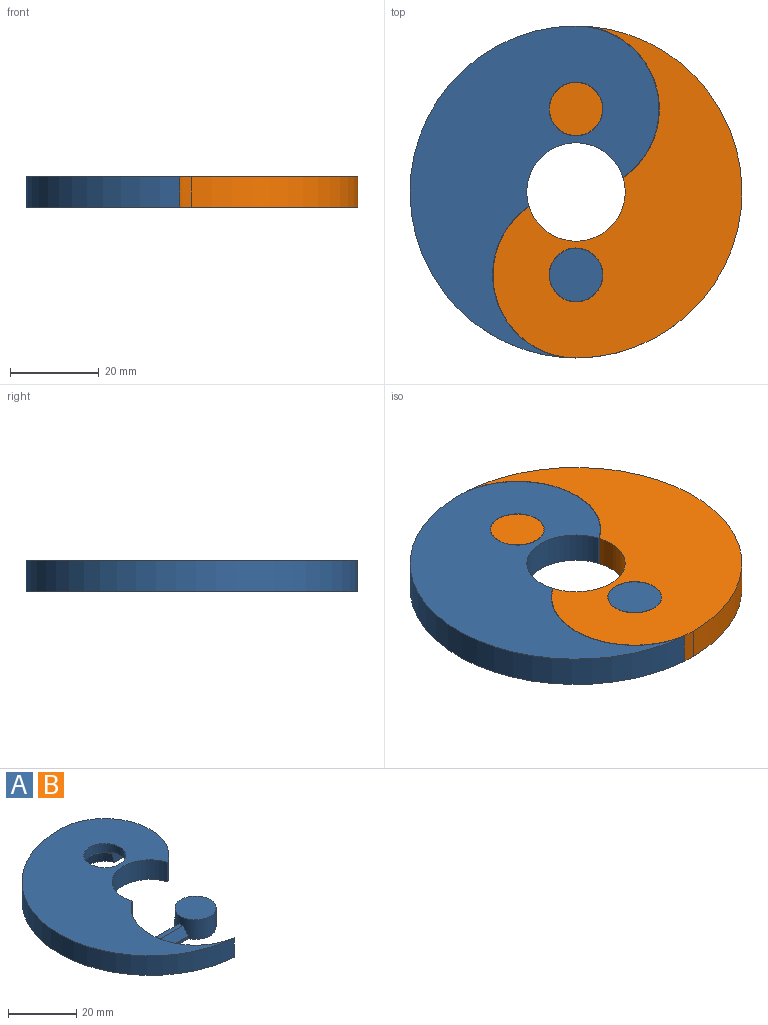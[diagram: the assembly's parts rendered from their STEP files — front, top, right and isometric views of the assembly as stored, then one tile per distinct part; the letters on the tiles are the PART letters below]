
ASSEMBLY  parts=2 mates=1
PART A: 28 faces, bbox 56.3x74.9x7 mm
  f0: plane 13.21x5.1mm, normal (0,0,-1), area 65.2mm2, adj f4,f11,f12,f27
  f1: plane 74.9x56.08mm, normal (0,0,-1), area 1974.4mm2, adj f3,f4,f5,f6,f8,f9,f11,f12
  f2: plane 74.9x56.25mm, normal (0,0,1), area 1893.9mm2, adj f3,f4,f5,f15,f18,f27
  f3: cylinder r=11.1mm len=21.7mm, axis (0,0,-1), area 244.1mm2, adj f1,f2,f4,f18
  f4: cylinder r=18.75mm len=34.21mm, axis (0,0,-1), area 312mm2, adj f0,f1,f2,f3,f5,f11,f12
  f5: cylinder r=37.5mm len=74.9mm, axis (0,0,-1), area 805.5mm2, adj f1,f2,f4,f15
  f6: cylinder r=6mm len=12mm, axis (0,0,-1), area 248.8mm2, adj f1,f7,f8,f9,f10,f13,f14
  f7: plane 12x12mm, normal (0,0,1), area 113.1mm2, adj f6
  f8: plane 13.13x1mm, normal (0,-1,0), area 13.1mm2, adj f1,f6,f14,f19
  f9: plane 13.13x1mm, normal (0,1,0), area 13.1mm2, adj f1,f6,f13,f17
  f10: plane 12.9x1.54mm, normal (0,0,1), area 19.8mm2, adj f6,f13,f14,f15,f16,f20
  f11: plane 13.14x4.2mm, normal (0,-1,0), area 53.2mm2, adj f0,f1,f4,f21,f23,f24
  f12: plane 13.14x4.2mm, normal (0,1,0), area 53.2mm2, adj f0,f1,f4,f21,f22,f25
  f13: plane 13.28x3mm, normal (0,0.87,0.5), area 44.8mm2, adj f6,f9,f10,f16
  f14: plane 13.28x3mm, normal (0,-0.87,0.5), area 44.8mm2, adj f6,f8,f10,f20
  f15: cylinder r=18.85mm len=34.2mm, axis (0,0,-1), area 301.1mm2, adj f1,f2,f5,f10,f16,f17,f18,f19
  f16: bspline ~3x1.75mm, area 0.3mm2, adj f10,f13,f15,f17
  f17: plane 1x0.1mm, normal (0.13,0.99,0), area 0.1mm2, adj f1,f9,f15,f16
  f18: plane 7x0.08mm, normal (-0.82,-0.57,0), area 0.7mm2, adj f1,f2,f3,f15
  f19: plane 1x0.1mm, normal (0.13,-0.99,0), area 0.1mm2, adj f1,f8,f15,f20
  f20: bspline ~3x1.75mm, area 0.3mm2, adj f10,f14,f15,f19
  f21: cone r=7mm half-angle=15deg, axis (0,0,-1), area 137.5mm2, adj f1,f11,f12,f26
  f22: plane 0.11x0.04mm, normal (0,0,1), area 0mm2, adj f12,f25,f27
  f23: plane 0.47x0.09mm, normal (-0.42,0.91,0), area 0mm2, adj f11,f24,f26,f27
  f24: plane 0.11x0.04mm, normal (0,0,1), area 0mm2, adj f11,f23,f27
  f25: plane 0.47x0.09mm, normal (-0.42,-0.91,0), area 0mm2, adj f12,f22,f26,f27
  f26: plane 12.2x11.62mm, normal (0,0,1), area 3.3mm2, adj f21,f23,f25,f27
  f27: cylinder r=6.1mm len=12.2mm, axis (0,0,-1), area 122.7mm2, adj f0,f2,f22,f23,f24,f25,f26
PART B: same geometry as A
PLACE A t=(35.07,15.88,19.33)mm
PLACE B rot(axis=(0,0,1),180deg) t=(35.07,15.88,19.33)mm
MATE fastened B.f6 <-> A.f4  axis (0,0,1) through (35.07,34.63,26.33)mm
